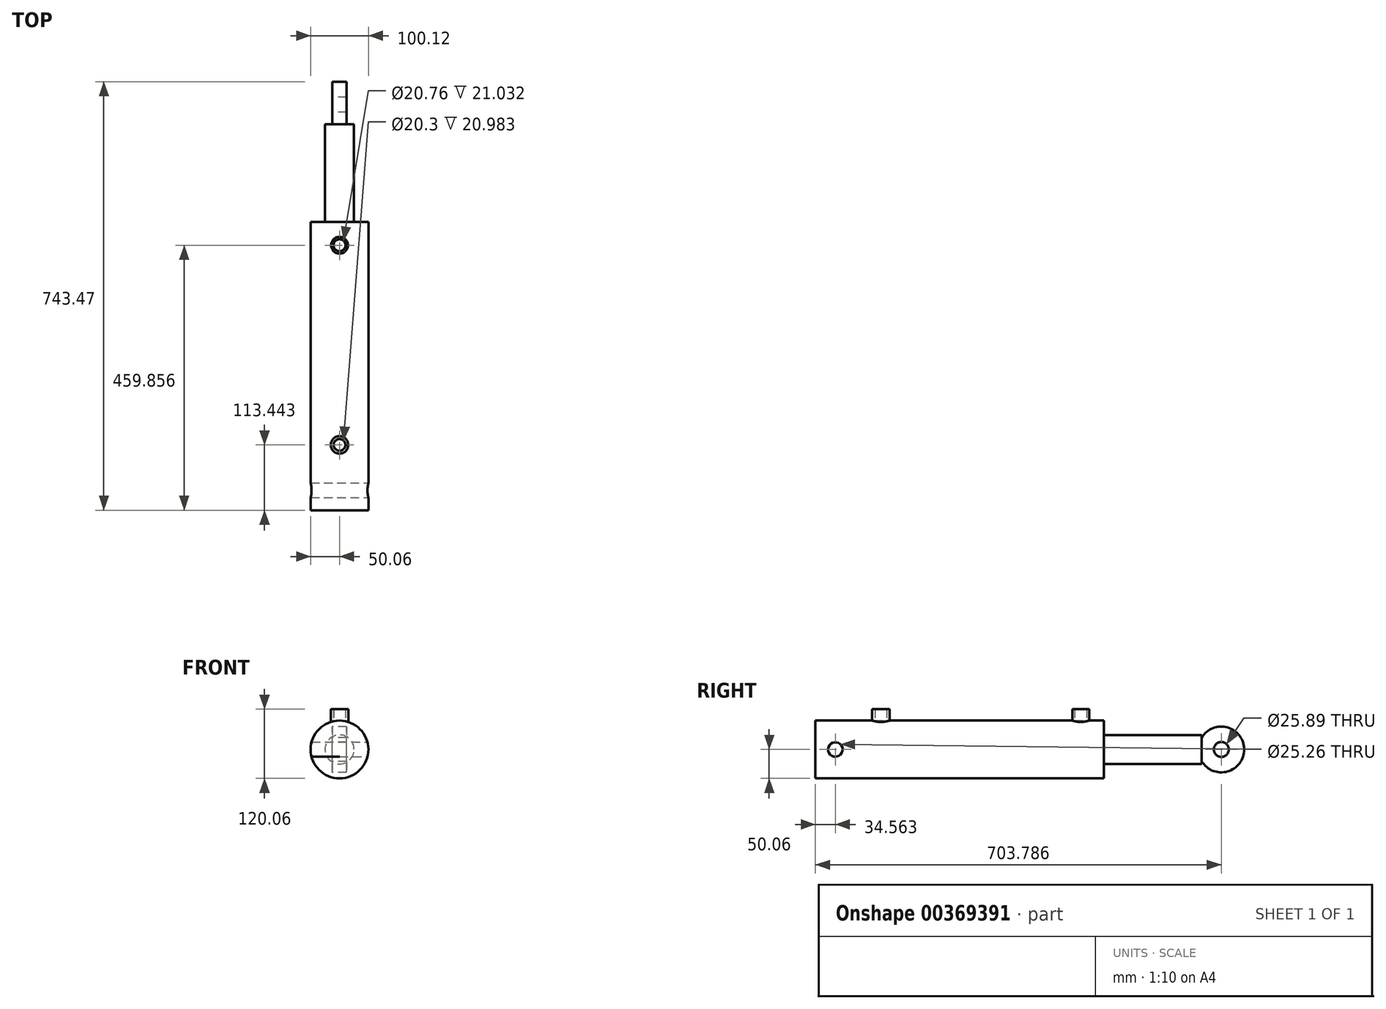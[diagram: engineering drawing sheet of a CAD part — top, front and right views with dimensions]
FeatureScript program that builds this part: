
annotation { "Feature Type Name" : "Feature", "Feature Type Description" : "" }
export const myFeature = defineFeature(function(context is Context, id is Id, definition is map)
    precondition{}
    {
        {
            var Q0;
            Q0=qCreatedBy(makeId("Front.planeOp"),FACE);
            var sketch = newSketch(context, id + "F0", { "sketchPlane" : qUnion([Q0])});
            skCircle(sketch, "E0", {"center": v(0, 0) * mm, "radius": 50.06 * mm});
            skSolve(sketch);
        }
        {
            var Q0;
            Q0 = qSketchRegion(id + "F0", true);
            extrude(context, id + "F1", {"entities" : qUnion([Q0]), "depth" : 500 * mm});
        }
        {
            var Q0;
            Q0=qCreatedBy(makeId("Front.planeOp"),FACE);
            var sketch = newSketch(context, id + "F2", { "sketchPlane" : qUnion([Q0])});
            skCircle(sketch, "E1", {"center": v(0, 0) * mm, "radius": 25.19 * mm});
            skSolve(sketch);
        }
        {
            var Q0;
            Q0 = qSketchRegion(id + "F2", true);
            extrude(context, id + "F3", {"entities" : qUnion([Q0]), "operationType" : NewBodyOperationType.ADD, "oppositeDirection" : true, "depth" : 170 * mm});
        }
        {
            var Q0;
            Q0=qCreatedBy(makeId("Right.planeOp"),FACE);
            var sketch = newSketch(context, id + "F4", { "sketchPlane" : qUnion([Q0])});
            skCircle(sketch, "E2", {"center": v(203.79, 0) * mm, "radius": 39.69 * mm});
            skCircle(sketch, "E3", {"center": v(203.79, 0) * mm, "radius": 12.95 * mm});
            skSolve(sketch);
        }
        {
            var Q0;
            Q0 = qSketchRegion(id + "F4", true);
            extrude(context, id + "F5", {"entities" : qUnion([Q0]), "operationType" : NewBodyOperationType.ADD, "endBound" : BoundingType.SYMMETRIC, "depth" : 25 * mm});
        }
        {
            var Q0;
            Q0=qCreatedBy(makeId("Right.planeOp"),FACE);
            var sketch = newSketch(context, id + "F6", { "sketchPlane" : qUnion([Q0])});
            skCircle(sketch, "E4", {"center": v(-465.44, 0) * mm, "radius": 12.63 * mm});
            skSolve(sketch);
        }
        {
            var Q0;
            Q0 = qSketchRegion(id + "F6", true);
            extrude(context, id + "F7", {"entities" : qUnion([Q0]), "operationType" : NewBodyOperationType.REMOVE, "endBound" : BoundingType.THROUGH_ALL, "oppositeDirection" : true, "depth" : 25 * mm, "hasSecondDirection" : true, "secondDirectionBound" : SecondDirectionBoundingType.THROUGH_ALL, "secondDirectionOppositeDirection" : false, "secondDirectionDepth" : 25 * mm});
        }
        {
            var Q0;
            Q0=qCreatedBy(makeId("Top.planeOp"),FACE);
            var sketch = newSketch(context, id + "F8", { "sketchPlane" : qUnion([Q0])});
            skCircle(sketch, "E5", {"center": v(0, -40.14) * mm, "radius": 14.58 * mm});
            skCircle(sketch, "E6", {"center": v(0, -40.14) * mm, "radius": 10.38 * mm});
            skSolve(sketch);
        }
        {
            var Q0;
            Q0 = qSketchRegion(id + "F8", true);
            extrude(context, id + "F9", {"entities" : qUnion([Q0]), "operationType" : NewBodyOperationType.ADD, "depth" : 70 * mm});
        }
        {
            var Q0;
            Q0=qCreatedBy(makeId("Top.planeOp"),FACE);
            var sketch = newSketch(context, id + "F10", { "sketchPlane" : qUnion([Q0])});
            skCircle(sketch, "E7", {"center": v(0, -386.56) * mm, "radius": 15.13 * mm});
            skCircle(sketch, "E8", {"center": v(0, -386.56) * mm, "radius": 10.15 * mm});
            skSolve(sketch);
        }
        {
            var Q0;
            Q0 = qSketchRegion(id + "F10", true);
            extrude(context, id + "F11", {"entities" : qUnion([Q0]), "operationType" : NewBodyOperationType.ADD, "depth" : 70 * mm});
        }
    });
